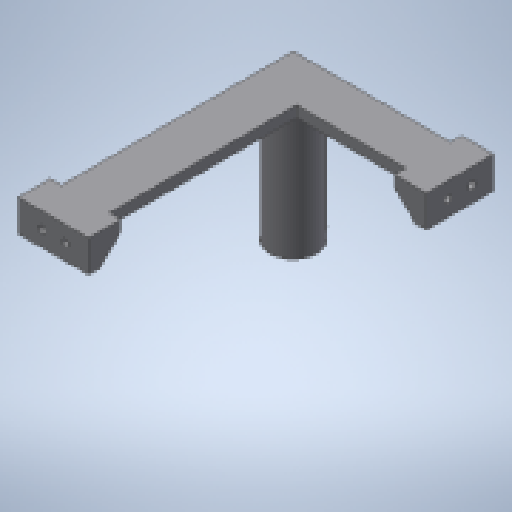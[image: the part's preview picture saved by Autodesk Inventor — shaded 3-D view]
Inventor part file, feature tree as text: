
AUTODESK INVENTOR PART (.ipt)
format: ipt  version: 2023 (Build 270158000, 158)  size: 339,968 bytes
history: native  units: mm
features: extrude x14, sketch x14, other x3, projected_geometry x2, mirror x1, reference x1
ambient origin geometry x8: Origin, YZ Plane, XZ Plane, XY Plane, X Axis, Y Axis, Z Axis, Center Point
bodies: Solid1 (feature_tree)
feature tree (35):
  extrude  "Extrusion1"  Depth=20.0mm
  extrude  "Extrusion2"  Depth=7.0mm
  sketch  "Sketch3"  dims[d4=30.0mm d5=0.0mm d6=80.0mm d7=7.0mm d8=0.0mm d9=0.0mm]
  extrude  "Extrusion3"  Depth=80.0mm TaperAngle=0.0deg
  extrude  "Extrusion4"  Depth=10.0mm
  extrude  "Extrusion5"  Depth=10.0mm
  extrude  "Extrusion6"  Depth=15.0mm
  extrude  "Extrusion7"  Depth=7.0mm TaperAngle=0.0deg
  extrude  "Extrusion8"  Depth=7.0mm TaperAngle=0.0deg
  extrude  "Extrusion9"  Depth=11.0mm
  extrude  "Extrusion10"  Depth=80.0mm
  extrude  "Extrusion11"  Depth=7.0mm TaperAngle=0.0deg
  extrude  "Extrusion12"  Depth=15.0mm
  extrude  "Extrusion13"  Depth=7.0mm TaperAngle=0.0deg
  mirror  "Mirror1"
  extrude  "Extrusion14"  TaperAngle=0.0deg  [1 undecoded]
  sketch  "Sketch1"  dims[d0=7.0mm d1=20.0mm]
  sketch  "Sketch2"  dims[d2=7.0mm d3=150.0mm]
  sketch  "Sketch4"  dims[d10=10.0mm d11=4.5mm]
  projected_geometry  "Projected Loop1"
  sketch  "Sketch5"  dims[d12=4.5mm d13=10.0mm]
  projected_geometry  "Projected Loop2"
  sketch  "Sketch6"  dims[d14=15.0mm d15=7.5mm]
  sketch  "Sketch7"  dims[d16=13.0mm d17=7.0mm d18=0.0mm]
  sketch  "Sketch8"  dims[d19=7.0mm d20=0.0mm d21=7.0mm d22=0.0mm]
  reference  "Reference1"
  sketch  "Sketch9"  dims[d23=11.0mm d24=11.0mm]
  sketch  "Sketch10"  dims[d25=12.0mm d26=0.0mm d27=80.0mm]
  sketch  "Sketch11"  dims[d28=7.0mm d29=72.0mm d30=0.0mm]
  sketch  "Sketch13"  dims[d31=0.0mm d32=15.0mm]
  sketch  "Sketch15"  dims[d33=20.0mm d34=7.0mm d35=0.0mm]
  sketch  "Sketch16"  dims[d36=7.0mm d37=0.0mm d38=7.0mm d39=7.0mm d40=13.0mm d41=7.0mm d42=0.0mm d43=0.0mm d44=45.0deg d45=7.0mm d46=0.0mm d47=7.0mm d48=0.0mm d49=10.0mm d50=10.0mm d51=15.0mm d52=6.5mm d53=6.507214mm d54=4.5mm d55=4.5mm d56=7.0mm d57=0.0mm d58=10.0mm d59=10.0mm d60=20.0mm d61=0.0mm d62=400.0mm d63=0.0mm]
  other  "<userpath>\OneDrive\ClawdDrive\Objet3D\3DPrinter\inventor\3DPrinterBeltCoreXY.iam"
  other  "3DPrinterBeltCoreXY.iam"
  other  "20X20 - T-slot - Vertical:2"
note: 1 required parameter value undecoded (feature->parameter linkage not recoverable at this tier; creation-order binding heuristic only, values carry confidence <= 0.55)
